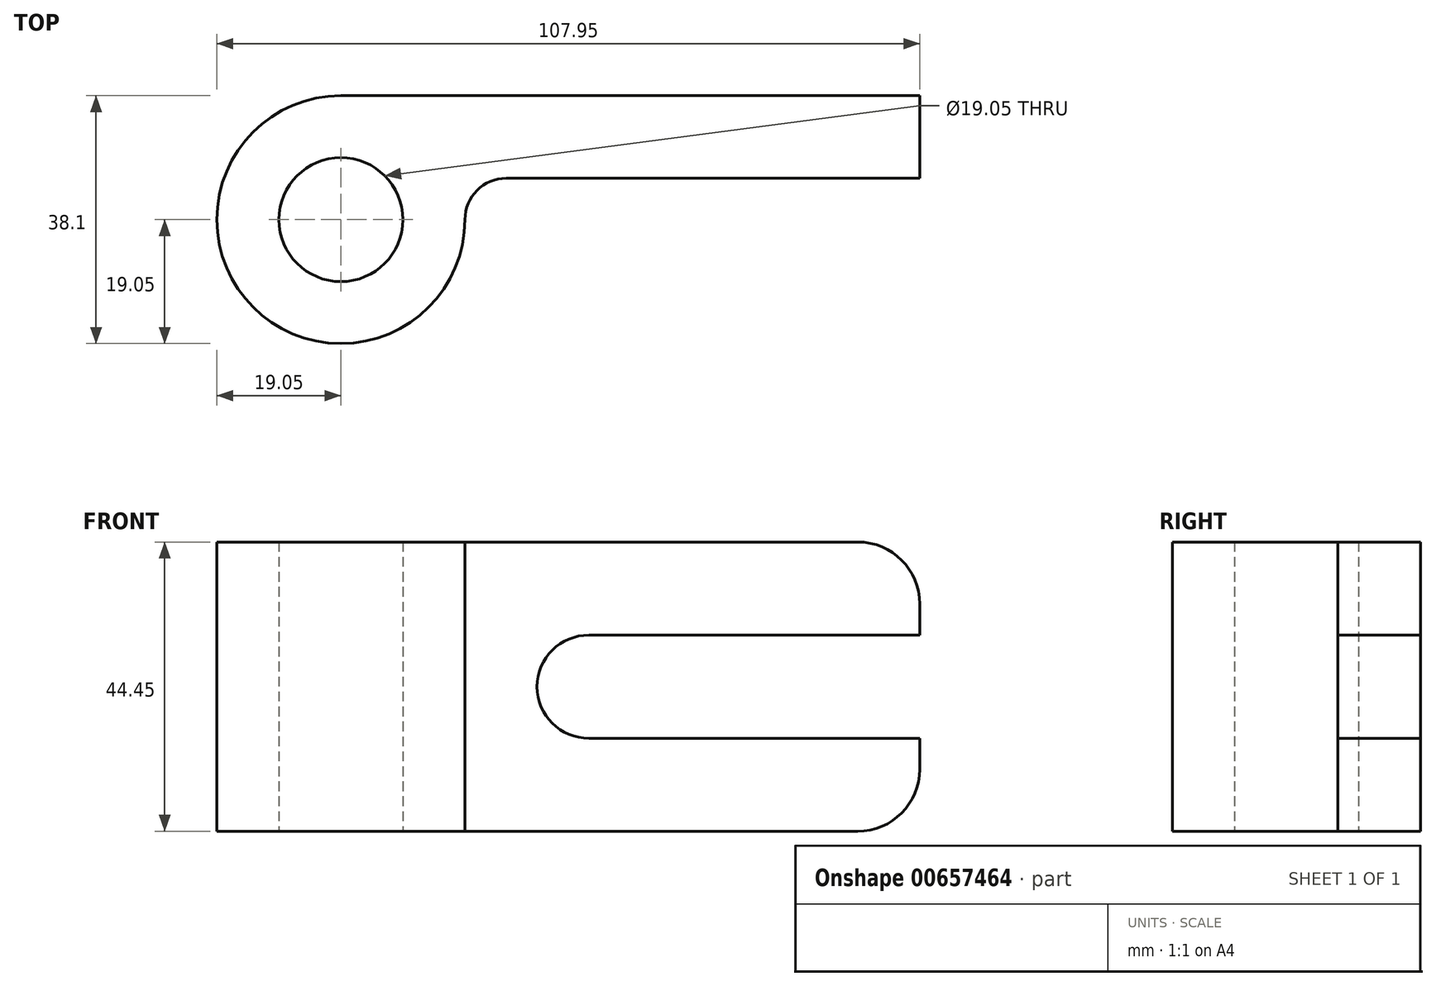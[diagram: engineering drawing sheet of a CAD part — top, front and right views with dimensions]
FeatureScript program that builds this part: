
annotation { "Feature Type Name" : "Feature", "Feature Type Description" : "" }
export const myFeature = defineFeature(function(context is Context, id is Id, definition is map)
    precondition{}
    {
        {
            var Q0;
            Q0=qCreatedBy(makeId("Top.planeOp"),FACE);
            var sketch = newSketch(context, id + "F0", { "sketchPlane" : qUnion([Q0])});
            skCircle(sketch, "E0", {"center": v(0, 0) * mm, "radius": 9.53 * mm});
            skCircle(sketch, "E1", {"center": v(0, 0) * mm, "radius": 19.05 * mm});
            skLineSegment(sketch, "E2", {"start": v(0, 19.05) * mm, "end": v(88.9, 19.05) * mm});
            skLineSegment(sketch, "E3", {"start": v(88.9, 19.05) * mm, "end": v(88.9, 6.35) * mm});
            skLineSegment(sketch, "E4", {"start": v(88.9, 6.35) * mm, "end": v(17.96, 6.35) * mm});
            skSolve(sketch);
        }
        {
            var Q0;
            {var subQ0=sQuery(id+"F0.wireOp",EDGE,"E2");Q0=makeQuery(id+"F0.imprint","IMPRINT",FACE,{"disambiguationData":[TD([[makeQuery(id+"F0.imprint","IMPRINT",EDGE,{"derivedFrom":subQ0}),-1.0]])]});}
            var Q1;
            Q1=makeQuery(id+"F0.imprint","IMPRINT",FACE,{"disambiguationData":[TD([[makeQuery(id+"F0.imprint","IMPRINT",EDGE,{"derivedFrom":sQuery(id+"F0.wireOp",EDGE,"E0")}),-1.0]])]});
            extrude(context, id + "F1", {"entities" : qUnion([Q0, Q1]), "depth" : 44.45 * mm, "offsetDistance" : 25.4 * mm});
        }
        {
            var Q0;
            Q0=makeQuery(id+"F1.opExtrude","SWEPT_EDGE",EDGE,{"disambiguationData":[OSD([sQuery(id+"F0.wireOp",EDGE,"E1"),sQuery(id+"F0.wireOp",EDGE,"E4")])]});
            fillet(context, id + "F2", {"entities" : qUnion([Q0]), "radius" : 6.35 * mm, "tangentPropagation" : true, "allowEdgeOverflow" : false});
        }
        {
            var Q0;
            Q0=makeQuery(id+"F1.opExtrude","CAP_EDGE",EDGE,{"disambiguationData":[OSD([sQuery(id+"F0.wireOp",EDGE,"E3")])],"isStart":false});
            var Q1;
            Q1=makeQuery(id+"F1.opExtrude","CAP_EDGE",EDGE,{"disambiguationData":[OSD([sQuery(id+"F0.wireOp",EDGE,"E3")])],"isStart":true});
            fillet(context, id + "F3", {"entities" : qUnion([Q0, Q1]), "radius" : 9.52 * mm, "tangentPropagation" : true, "allowEdgeOverflow" : false});
        }
        {
            var Q0;
            Q0=makeQuery(id+"F1.opExtrude","SWEPT_FACE",FACE,{"disambiguationData":[OSD([sQuery(id+"F0.wireOp",EDGE,"E4")])]});
            var sketch = newSketch(context, id + "F4", { "sketchPlane" : qUnion([Q0])});
            skLineSegment(sketch, "E5.top", {"start": v(88.9, 30.14) * mm, "end": v(30.12, 30.14) * mm});
            skLineSegment(sketch, "E5.left", {"start": v(88.9, 14.26) * mm, "end": v(88.9, 30.14) * mm});
            skLineSegment(sketch, "E5.right", {"start": v(30.12, 14.26) * mm, "end": v(30.12, 30.14) * mm});
            skLineSegment(sketch, "E6", {"start": v(30.12, 14.26) * mm, "end": v(88.9, 14.26) * mm});
            skSolve(sketch);
        }
        {
            var Q0;
            Q0=makeQuery(id+"F4.imprint","IMPRINT",FACE,{"disambiguationData":[TD([[makeQuery(id+"F4.imprint","IMPRINT",EDGE,{"derivedFrom":sQuery(id+"F4.wireOp",EDGE,"E5.top")}),1.0]])]});
            extrude(context, id + "F5", {"entities" : qUnion([Q0]), "operationType" : NewBodyOperationType.REMOVE, "oppositeDirection" : true, "depth" : 25.4 * mm, "offsetDistance" : 25.4 * mm});
        }
        {
            var Q0;
            Q0=makeQuery(id+"F5.boolean.opBoolean","COPY",EDGE,{"derivedFrom":makeQuery(id+"F5.opExtrude","SWEPT_EDGE",EDGE,{"disambiguationData":[OSD([sQuery(id+"F4.wireOp",EDGE,"E5.top"),sQuery(id+"F4.wireOp",EDGE,"E5.right")])]})});
            var Q1;
            Q1=makeQuery(id+"F5.boolean.opBoolean","COPY",EDGE,{"derivedFrom":makeQuery(id+"F5.opExtrude","SWEPT_EDGE",EDGE,{"disambiguationData":[OSD([sQuery(id+"F4.wireOp",EDGE,"E5.right"),sQuery(id+"F4.wireOp",EDGE,"E6")])]})});
            fillet(context, id + "F6", {"entities" : qUnion([Q0, Q1]), "radius" : 7.98 * mm, "tangentPropagation" : true, "allowEdgeOverflow" : false});
        }
    });
